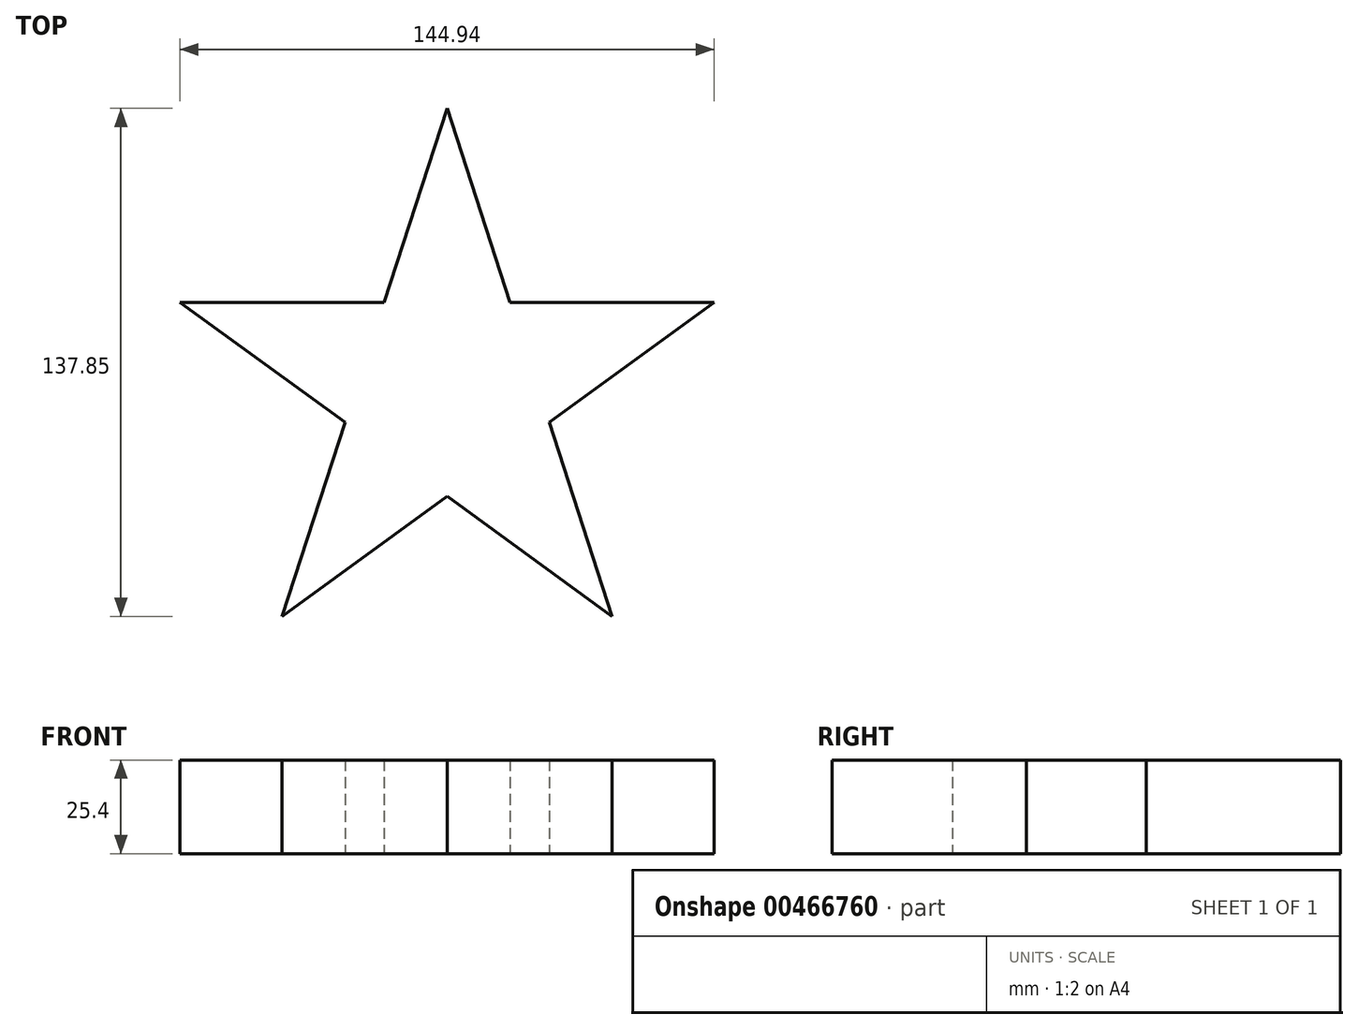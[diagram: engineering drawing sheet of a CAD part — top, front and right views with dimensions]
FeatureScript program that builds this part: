
annotation { "Feature Type Name" : "Feature", "Feature Type Description" : "" }
export const myFeature = defineFeature(function(context is Context, id is Id, definition is map)
    precondition{}
    {
        {
            var Q0;
            Q0=qCreatedBy(makeId("Top.planeOp"),FACE);
            var sketch = newSketch(context, id + "F0", { "sketchPlane" : qUnion([Q0])});
            skCircle(sketch, "E0", {"center": v(0, 0) * mm, "radius": 76.2 * mm});
            skCircle(sketch, "E1.cCircle", {"center": v(0, 0) * mm, "radius": 76.2 * mm, "construction": true});
            skLineSegment(sketch, "E1.0", {"start": v(44.79, -61.65) * mm, "end": v(-44.79, -61.65) * mm});
            skLineSegment(sketch, "E1.1", {"start": v(-44.79, -61.65) * mm, "end": v(-72.47, 23.55) * mm});
            skLineSegment(sketch, "E1.2", {"start": v(-72.47, 23.55) * mm, "end": v(0, 76.2) * mm});
            skLineSegment(sketch, "E1.3", {"start": v(0, 76.2) * mm, "end": v(72.47, 23.55) * mm});
            skLineSegment(sketch, "E1.4", {"start": v(72.47, 23.55) * mm, "end": v(44.79, -61.65) * mm});
            skPoint(sketch, "E2", {"position": v(-44.79, 61.65) * mm});
            skLineSegment(sketch, "E3", {"start": v(-44.79, 61.65) * mm, "end": v(-72.47, 23.55) * mm});
            skLineSegment(sketch, "E4", {"start": v(-44.79, 61.65) * mm, "end": v(0, 76.2) * mm});
            skLineSegment(sketch, "E5", {"start": v(-44.79, 61.65) * mm, "end": v(0, 0) * mm});
            skPoint(sketch, "E6", {"position": v(-17.1, 23.55) * mm});
            skLineSegment(sketch, "E7", {"start": v(-17.1, 23.55) * mm, "end": v(-72.47, 23.55) * mm});
            skLineSegment(sketch, "E8", {"start": v(-17.1, 23.55) * mm, "end": v(0, 76.2) * mm});
            skLineSegment(sketch, "E9.1.0", {"start": v(-27.68, -9) * mm, "end": v(-72.47, 23.55) * mm});
            skLineSegment(sketch, "E9.1.1", {"start": v(-27.68, -9) * mm, "end": v(-44.79, -61.65) * mm});
            skLineSegment(sketch, "E9.2.0", {"start": v(0, -29.1) * mm, "end": v(-44.79, -61.65) * mm});
            skLineSegment(sketch, "E9.2.1", {"start": v(0, -29.1) * mm, "end": v(44.79, -61.65) * mm});
            skLineSegment(sketch, "E9.3.0", {"start": v(27.68, -9) * mm, "end": v(44.79, -61.65) * mm});
            skLineSegment(sketch, "E9.3.1", {"start": v(27.68, -9) * mm, "end": v(72.47, 23.55) * mm});
            skLineSegment(sketch, "E9.4.0", {"start": v(17.1, 23.55) * mm, "end": v(72.47, 23.55) * mm});
            skLineSegment(sketch, "E9.4.1", {"start": v(17.1, 23.55) * mm, "end": v(0, 76.2) * mm});
            skSolve(sketch);
        }
        {
            var Q0;
            Q0=makeQuery(id+"F0.imprint","IMPRINT",FACE,{"disambiguationData":[TD([[makeQuery(id+"F0.imprint","IMPRINT",EDGE,{"derivedFrom":sQuery(id+"F0.wireOp",EDGE,"E7")}),1.0]])]});
            extrude(context, id + "F1", {"entities" : qUnion([Q0]), "depth" : 25.4 * mm});
        }
    });
